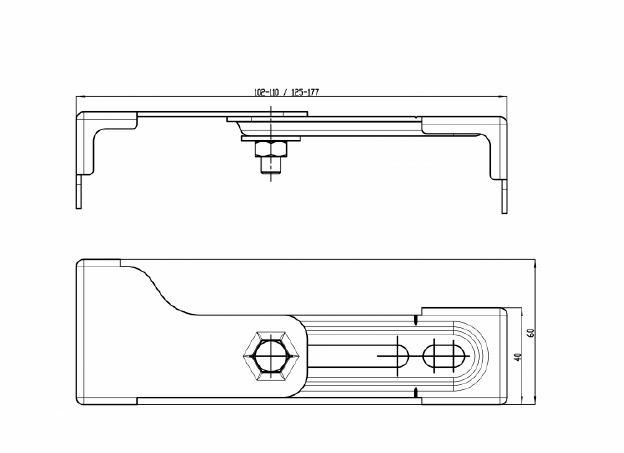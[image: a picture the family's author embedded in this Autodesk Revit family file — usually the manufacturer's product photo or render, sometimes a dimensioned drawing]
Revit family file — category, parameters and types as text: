
# Revit family: PRD_AR_GlvnzdStlBrckts_AquafixWallBrackets_ZCMPX140
name_source: partatom
category: Specialty Equipment
revit_build: Autodesk Revit 2018 (Build: 20190510_1515(x64)
units: mm (PartAtom-declared; Revit-internal decimal feet)

## family parameters
Always vertical = No
Cut with Voids When Loaded = No
OmniClass Number = 23.40.20.21
OmniClass Title = Toilet and Bath Specialties
Part Type = Normal
Room Calculation Point = No
Round Connector Dimension = Use Diameter
Shared = Yes
Work Plane-Based = No

## types (1)
- PRD_AR_GlvnzdStlBrckts_AquafixWallBrackets_ZCMPX140
    AssetType = Fixed
    BIMObjectName = PRD_AR_GlvnzdStlBrckts_AquafixWallBrackets_ZCMPX140
    BracketMaterial = PRD_AR_GalvanizedSteel
    Category = Pr_20_85_09_33, Galvanized Steel Brackets
    Color = galvanized steel
    Description = AQUAFIX wall brackets for pre-wall installation, for fastening AQUAFIX installation elements on masonry or in front of the single plank wall, continuously adjustable in depth, for individual mounting, galvanized steel, included fixing material, packaging unit 2 pieces.
    Description_2 = AQUAFIX wall brackets for pre-wall installation, for fastening AQUAFIX installation elements on masonry or in front of the single plank
wall, continuously adjustable in depth, for individual mounting, galvanized steel, included fixing material, packaging unit 2 pieces.
    DurationUnit = year
    Features = galvanized steel, included fixing material
    FillingQuantity = 2
    Finish = galvanized
    Form = Wall-mounted
    GrossWeight = 0.50 kg
    IfcExportAs = IfcFurnitureType
    IfcExportType = USERDEFINED
    MainColor = galvanized steel
    Manufacturer = KWC Group AG
    ManufacturerName = KWC Group AG
    ManufacturerURL = www.kwc.com
    Material = galvanized steel
    Model = ZCMPX140
    ModelNumber = 2000100867
    ModelReference = ZCMPX140
    NBSDescription = Galvanized steel brackets
    NBSReference = 45-70-05/370
    Name = AQUAFIX wall brackets ZCMPX140
    NetWeight = 0.48 kg
    NominalDepth = 177 mm
    NominalHeight = 40 mm  [stored 0.131234 ft]
    NominalWidth = 60 mm  [stored 0.19685 ft]
    ProductInformation = https://pim.kwc.com
    Size = 60 x 40 x 177 mm
    URL = www.kwc.com
    Uniclass2015Code = Pr_20_85_09_33
    Uniclass2015Title = Galvanized steel brackets
    Uniclass2015Version = Products v1.10
    Version = 1
    WarrantyDurationUnit = year

note: [stored X ft] marks values corroborated as IEEE doubles in the binary element streams (Revit-internal decimal feet)

## geometry (parser evidence)
native form markers: Sweep x6
no freeform markers — native parametric forms only
